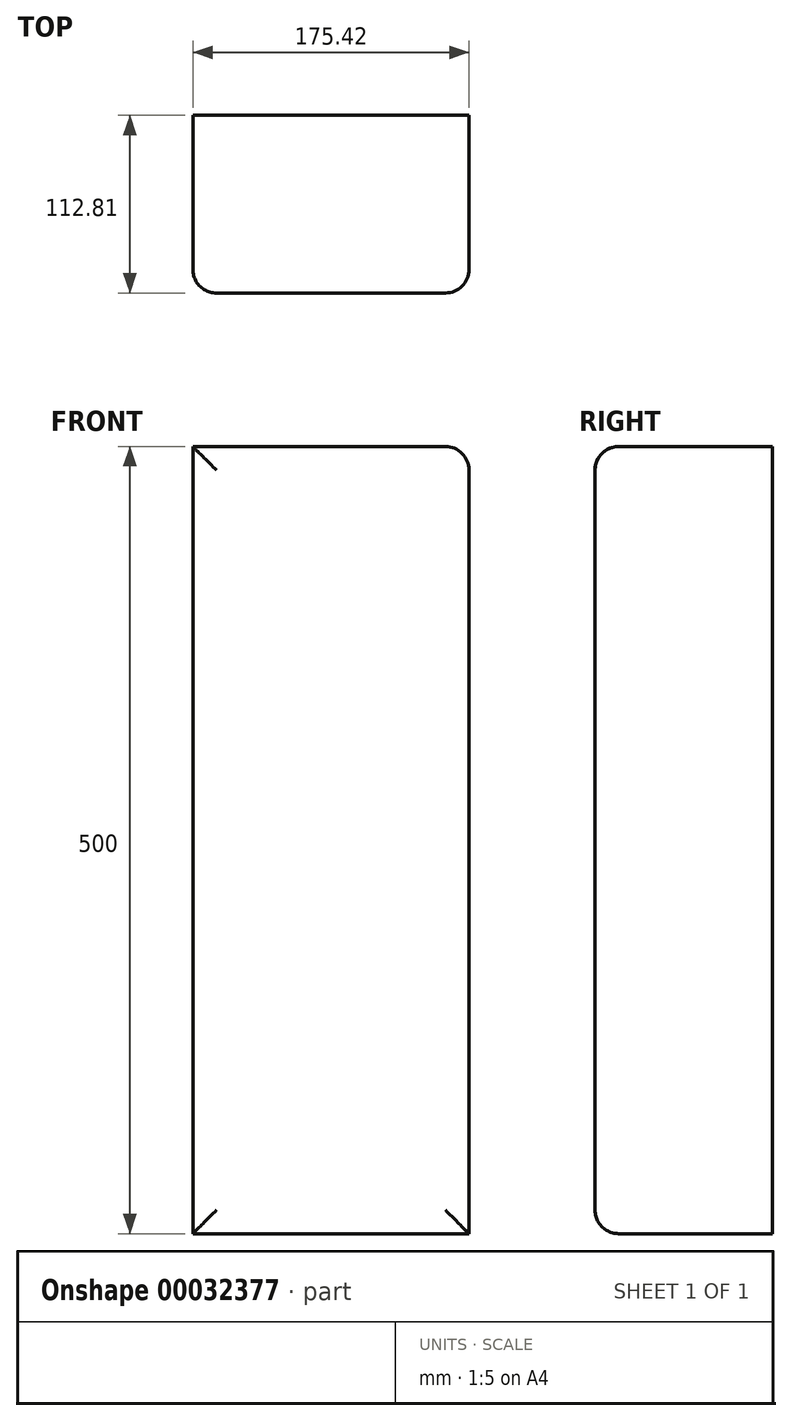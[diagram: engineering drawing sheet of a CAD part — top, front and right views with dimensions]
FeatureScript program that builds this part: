
annotation { "Feature Type Name" : "Feature", "Feature Type Description" : "" }
export const myFeature = defineFeature(function(context is Context, id is Id, definition is map)
    precondition{}
    {
        {
            var Q0;
            Q0=qCreatedBy(makeId("Top.planeOp"),FACE);
            var sketch = newSketch(context, id + "F0", { "sketchPlane" : qUnion([Q0])});
            skLineSegment(sketch, "E0.bottom", {"start": v(0, 0) * mm, "end": v(175.42, 0) * mm});
            skLineSegment(sketch, "E0.top", {"start": v(0, -112.81) * mm, "end": v(175.42, -112.81) * mm});
            skLineSegment(sketch, "E0.left", {"start": v(0, 0) * mm, "end": v(0, -112.81) * mm});
            skLineSegment(sketch, "E0.right", {"start": v(175.42, 0) * mm, "end": v(175.42, -112.81) * mm});
            skSolve(sketch);
        }
        {
            var Q0;
            Q0 = qSketchRegion(id + "F0", true);
            var Q1;
            Q1=makeQuery(id+"F0.imprint","IMPRINT",FACE,{"disambiguationData":[TD([[makeQuery(id+"F0.imprint","IMPRINT",EDGE,{"derivedFrom":sQuery(id+"F0.wireOp",EDGE,"E0.bottom")}),-1.0]])]});
            extrude(context, id + "F1", {"entities" : qUnion([Q0, Q1]), "depth" : 500 * mm});
        }
        {
            var Q0;
            Q0=makeQuery(id+"F1.opExtrude","CAP_EDGE",EDGE,{"disambiguationData":[OSD([sQuery(id+"F0.wireOp",EDGE,"E0.top")])],"isStart":false});
            var Q1;
            Q1=makeQuery(id+"F1.opExtrude","SWEPT_FACE",FACE,{"disambiguationData":[OSD([sQuery(id+"F0.wireOp",EDGE,"E0.top")])]});
            var Q2;
            Q2=makeQuery(id+"F1.opExtrude","SWEPT_EDGE",EDGE,{"disambiguationData":[OSD([sQuery(id+"F0.wireOp",EDGE,"E0.top"),sQuery(id+"F0.wireOp",EDGE,"E0.right")])]});
            var Q3;
            Q3=makeQuery(id+"F1.opExtrude","CAP_EDGE",EDGE,{"disambiguationData":[OSD([sQuery(id+"F0.wireOp",EDGE,"E0.right")])],"isStart":false});
            fillet(context, id + "F2", {"entities" : qUnion([Q0, Q1, Q2, Q3]), "radius" : 15 * mm, "tangentPropagation" : true, "allowEdgeOverflow" : false});
        }
    });
